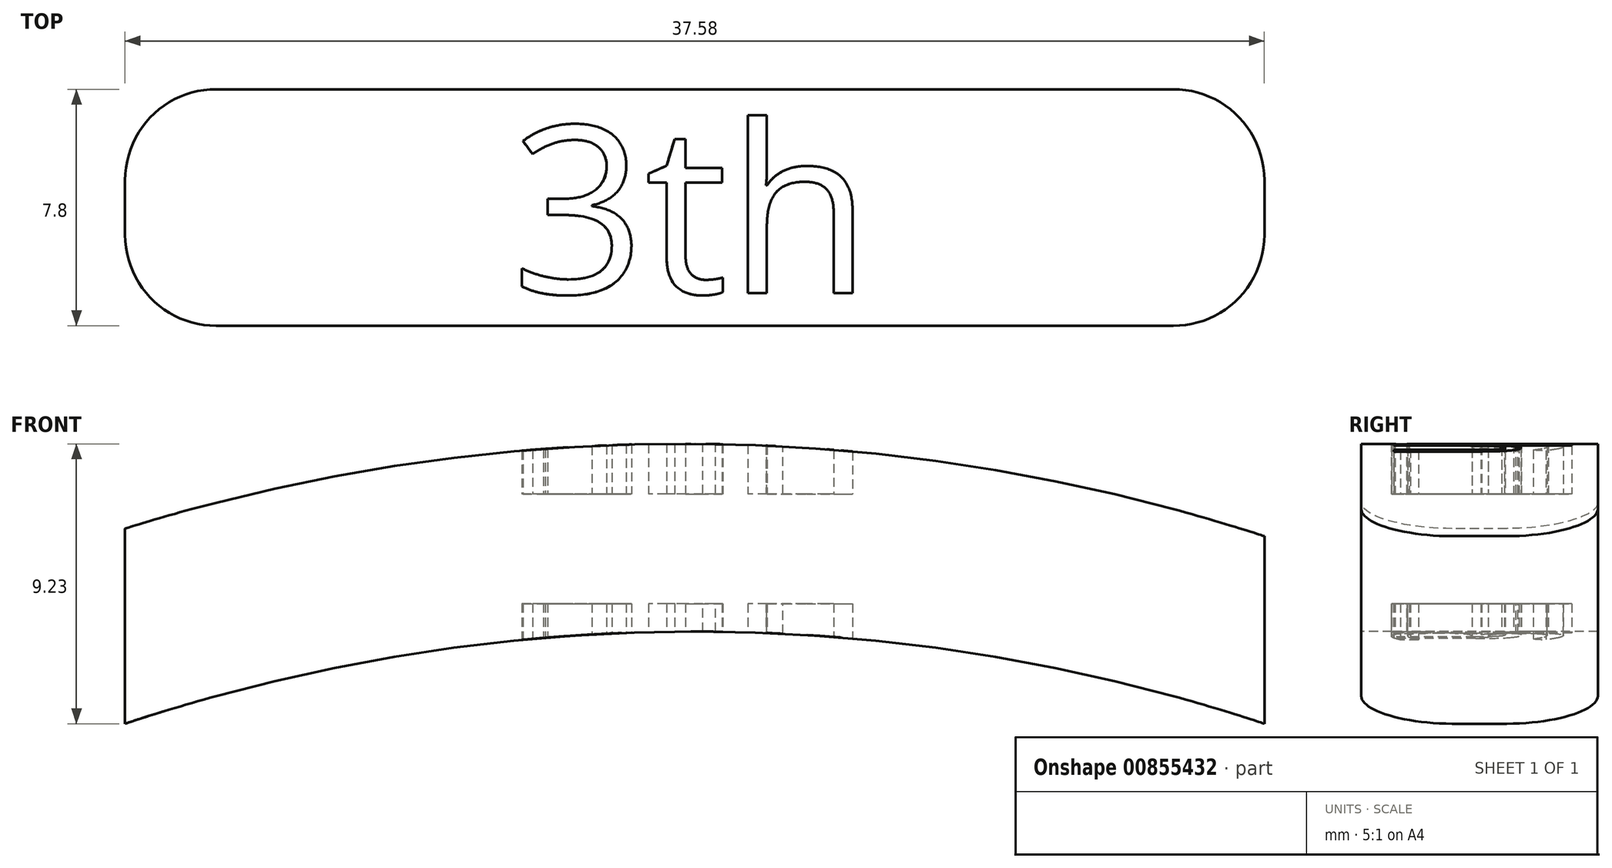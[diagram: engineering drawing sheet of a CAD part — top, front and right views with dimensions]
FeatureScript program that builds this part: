
annotation { "Feature Type Name" : "Feature", "Feature Type Description" : "" }
export const myFeature = defineFeature(function(context is Context, id is Id, definition is map)
    precondition{}
    {
        {
            var Q0;
            Q0=qCreatedBy(makeId("Top.planeOp"),FACE);
            var sketch = newSketch(context, id + "F0", { "sketchPlane" : qUnion([Q0])});
            skLineSegment(sketch, "E0.bottom", {"start": v(0, 0) * mm, "end": v(37.58, 0) * mm});
            skLineSegment(sketch, "E0.top", {"start": v(0, -7.8) * mm, "end": v(37.58, -7.8) * mm});
            skLineSegment(sketch, "E0.left", {"start": v(0, 0) * mm, "end": v(0, -7.8) * mm});
            skLineSegment(sketch, "E0.right", {"start": v(37.58, 0) * mm, "end": v(37.58, -7.8) * mm});
            skSolve(sketch);
        }
        {
            var Q0;
            Q0 = qSketchRegion(id + "F0", true);
            extrude(context, id + "F1", {"entities" : qUnion([Q0]), "depth" : 9.3 * mm, "offsetDistance" : 25 * mm});
        }
        {
            var Q0;
            Q0=makeQuery(id+"F1.opExtrude","SWEPT_FACE",FACE,{"disambiguationData":[OSD([sQuery(id+"F0.wireOp",EDGE,"E0.top")])]});
            var sketch = newSketch(context, id + "F2", { "sketchPlane" : qUnion([Q0])});
            skArc(sketch, "E1", {"start": v(37.58, 0) * mm, "mid": v(18.8, 3.04) * mm, "end": v(0, 0) * mm});
            skArc(sketch, "E2", {"start": v(37.58, 6.19) * mm, "mid": v(18.81, 9.23) * mm, "end": v(0, 6.44) * mm});
            skLineSegment(sketch, "E3", {"start": v(37.58, 6.19) * mm, "end": v(37.58, 0) * mm});
            skLineSegment(sketch, "E4", {"start": v(0, 6.44) * mm, "end": v(0, 0) * mm});
            skSolve(sketch);
        }
        {
            var Q0;
            Q0 = qSketchRegion(id + "F2", true);
            extrude(context, id + "F3", {"entities" : qUnion([Q0]), "operationType" : NewBodyOperationType.INTERSECT, "oppositeDirection" : true, "depth" : 36.9 * mm, "offsetDistance" : 25 * mm});
        }
        {
            var Q0;
            Q0=makeQuery(id+"F1.opExtrude","SWEPT_EDGE",EDGE,{"disambiguationData":[OSD([sQuery(id+"F0.wireOp",EDGE,"E0.top"),sQuery(id+"F0.wireOp",EDGE,"E0.right")])]});
            var Q1;
            Q1=makeQuery(id+"F1.opExtrude","SWEPT_EDGE",EDGE,{"disambiguationData":[OSD([sQuery(id+"F0.wireOp",EDGE,"E0.bottom"),sQuery(id+"F0.wireOp",EDGE,"E0.right")])]});
            var Q2;
            Q2=makeQuery(id+"F1.opExtrude","SWEPT_EDGE",EDGE,{"disambiguationData":[OSD([sQuery(id+"F0.wireOp",EDGE,"E0.bottom"),sQuery(id+"F0.wireOp",EDGE,"E0.left")])]});
            var Q3;
            Q3=makeQuery(id+"F1.opExtrude","SWEPT_EDGE",EDGE,{"disambiguationData":[OSD([sQuery(id+"F0.wireOp",EDGE,"E0.top"),sQuery(id+"F0.wireOp",EDGE,"E0.left")])]});
            fillet(context, id + "F4", {"entities" : qUnion([Q0, Q1, Q2, Q3]), "radius" : 3 * mm, "tangentPropagation" : true, "allowEdgeOverflow" : false});
        }
        {
            var Q0;
            Q0=qCreatedBy(makeId("Top.planeOp"),FACE);
            var sketch = newSketch(context, id + "F5", { "sketchPlane" : qUnion([Q0])});
            skText(sketch, "E5", { "text": "3th", "fontName": "OpenSans-Regular.ttf"});
            const initialGuessF5  = {"E5": [0.01274, -0.00673, 1, 0, 0.00556]};
            skSetInitialGuess(sketch, initialGuessF5);
            skSolve(sketch);
        }
        {
            var Q0;
            Q0 = qSketchRegion(id + "F5", true);
            extrude(context, id + "F6", {"entities" : qUnion([Q0]), "operationType" : NewBodyOperationType.REMOVE, "depth" : 31.8 * mm, "offsetDistance" : 25 * mm});
        }
        {
            var Q0;
            Q0=makeQuery(id+"F1.opExtrude","SWEPT_FACE",FACE,{"disambiguationData":[OSD([sQuery(id+"F0.wireOp",EDGE,"E0.bottom")])]});
            var sketch = newSketch(context, id + "F7", { "sketchPlane" : qUnion([Q0])});
            skLineSegment(sketch, "E6.bottom", {"start": v(-27.91, 7.58) * mm, "end": v(-8.68, 7.58) * mm});
            skLineSegment(sketch, "E6.top", {"start": v(-27.91, 3.96) * mm, "end": v(-8.68, 3.96) * mm});
            skLineSegment(sketch, "E6.left", {"start": v(-27.91, 7.58) * mm, "end": v(-27.91, 3.96) * mm});
            skLineSegment(sketch, "E6.right", {"start": v(-8.68, 7.58) * mm, "end": v(-8.68, 3.96) * mm});
            skSolve(sketch);
        }
        {
            var Q0;
            Q0 = qSketchRegion(id + "F7", true);
            extrude(context, id + "F8", {"entities" : qUnion([Q0]), "operationType" : NewBodyOperationType.ADD, "oppositeDirection" : true, "depth" : 7.7 * mm, "offsetDistance" : 25 * mm});
        }
    });
